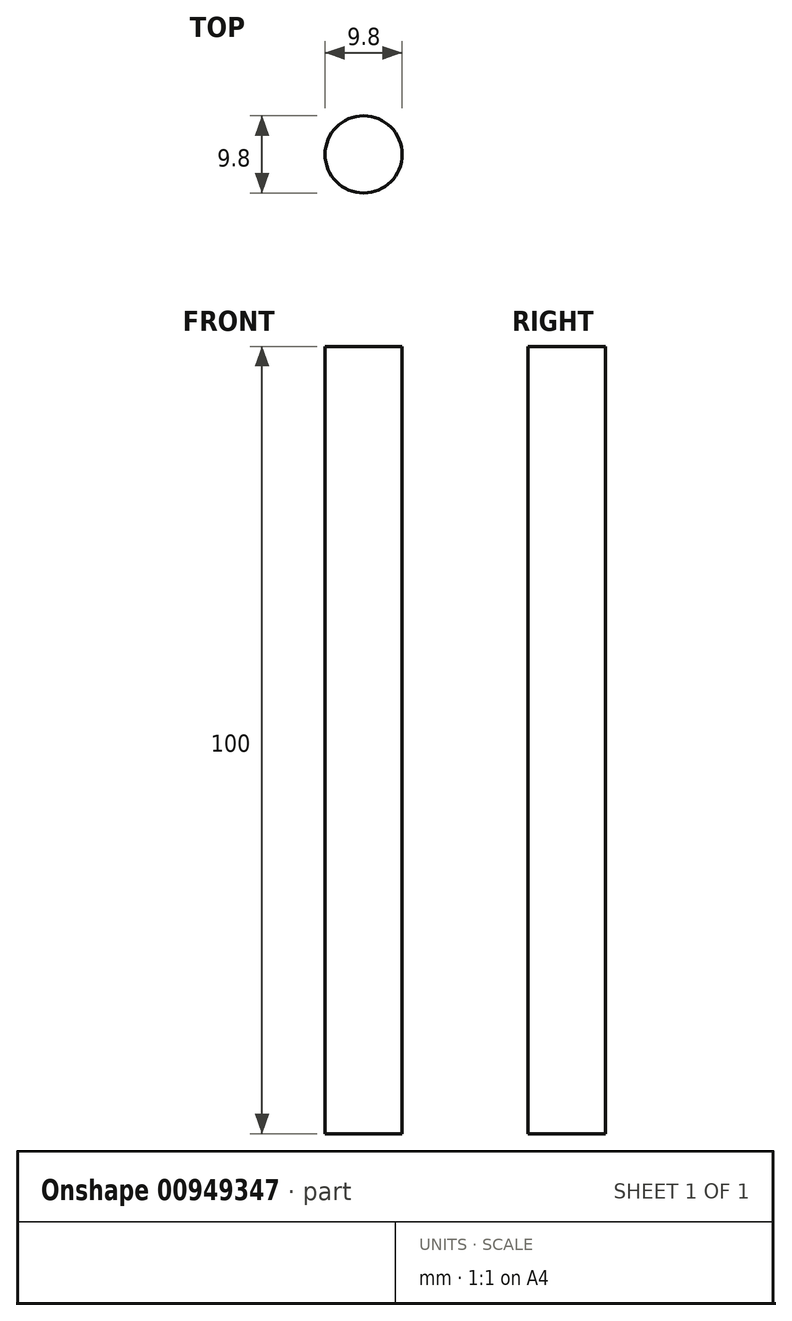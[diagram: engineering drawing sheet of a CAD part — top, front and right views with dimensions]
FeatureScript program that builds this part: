
annotation { "Feature Type Name" : "Feature", "Feature Type Description" : "" }
export const myFeature = defineFeature(function(context is Context, id is Id, definition is map)
    precondition{}
    {
        {
            var Q0;
            Q0=qCreatedBy(makeId("Top.planeOp"),FACE);
            var sketch = newSketch(context, id + "F0", { "sketchPlane" : qUnion([Q0])});
            skCircle(sketch, "E0", {"center": v(0, 0) * mm, "radius": 4.9 * mm});
            skSolve(sketch);
        }
        {
            var Q0;
            Q0=makeQuery(id+"F0.imprint","IMPRINT",FACE,{"disambiguationData":[TD([[makeQuery(id+"F0.imprint","IMPRINT",EDGE,{"derivedFrom":sQuery(id+"F0.wireOp",EDGE,"E0")}),1.0]])]});
            extrude(context, id + "F1", {"entities" : qUnion([Q0]), "depth" : 100 * mm, "offsetDistance" : 25 * mm});
        }
    });
